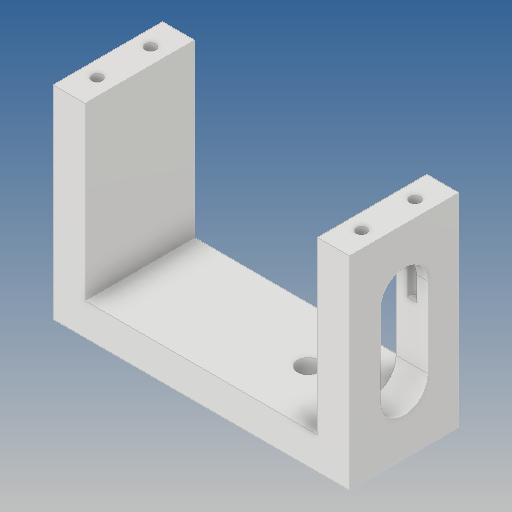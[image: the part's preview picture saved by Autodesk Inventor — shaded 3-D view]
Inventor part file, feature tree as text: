
AUTODESK INVENTOR PART (.ipt)
format: ipt  version: 2020 (Build 240168000, 168)  size: 158,208 bytes
history: native  units: mm
features: extrude x5, sketch x5, other x1
ambient origin geometry x8: Origin, YZ Plane, XZ Plane, XY Plane, X Axis, Y Axis, Z Axis, Center Point
bodies: Body1 (feature_tree)
feature tree (11):
  other  "Твердое тело1"
  extrude  "Выдавливание1"  Depth=38.0mm
  extrude  "Выдавливание2"  Depth=6.0mm
  extrude  "Выдавливание3"  Depth=6.0mm
  extrude  "Выдавливание4"  Depth=6.0mm
  extrude  "Выдавливание5"  Depth=38.0mm
  sketch  "Эскиз1"
  sketch  "Эскиз2"
  sketch  "Эскиз3"
  sketch  "Эскиз4"
  sketch  "Эскиз5"
